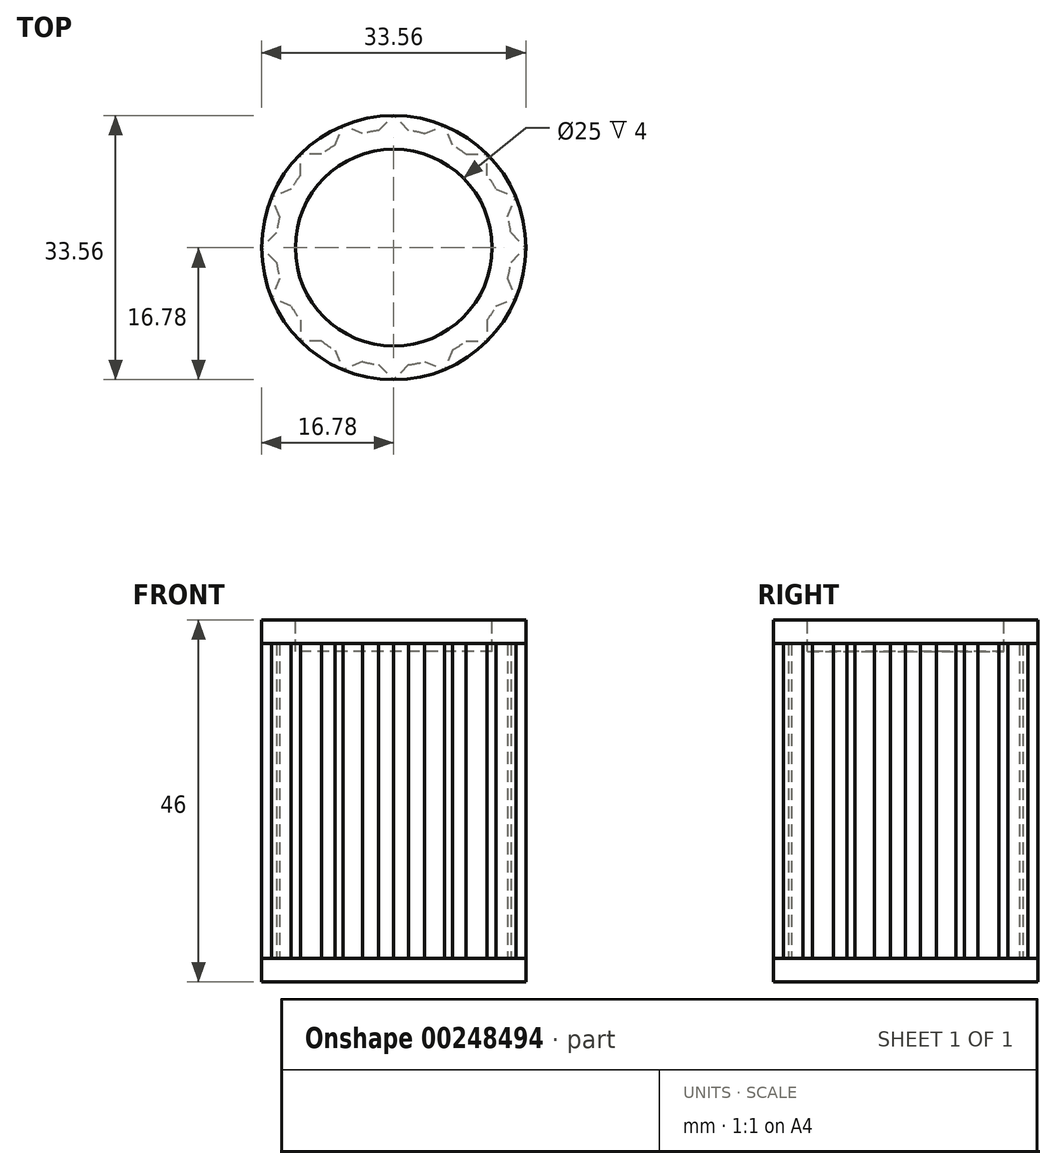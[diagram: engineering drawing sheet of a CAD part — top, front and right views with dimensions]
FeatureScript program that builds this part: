
annotation { "Feature Type Name" : "Feature", "Feature Type Description" : "" }
export const myFeature = defineFeature(function(context is Context, id is Id, definition is map)
    precondition{}
    {
        {
            var Q0;
            Q0=qCreatedBy(makeId("Top.planeOp"),FACE);
            var sketch = newSketch(context, id + "F0", { "sketchPlane" : qUnion([Q0])});
            skCircle(sketch, "E0", {"center": v(0, 0) * mm, "radius": 15 * mm});
            skLineSegment(sketch, "E1", {"start": v(14.28, 0) * mm, "end": v(14.28, 2.5) * mm});
            skLineSegment(sketch, "E2", {"start": v(14.28, 2.5) * mm, "end": v(16.78, 0) * mm});
            skLineSegment(sketch, "E3.MirrorCS", {"start": v(14.28, 0) * mm, "end": v(14.28, -2.5) * mm});
            skLineSegment(sketch, "E4.MirrorCS", {"start": v(14.28, -2.5) * mm, "end": v(16.78, 0) * mm});
            skLineSegment(sketch, "E5.1.0", {"start": v(12.24, 7.77) * mm, "end": v(15.5, 6.42) * mm});
            skLineSegment(sketch, "E5.1.1", {"start": v(14.15, 3.15) * mm, "end": v(15.5, 6.42) * mm});
            skLineSegment(sketch, "E5.1.2", {"start": v(13.2, 5.46) * mm, "end": v(14.15, 3.15) * mm});
            skLineSegment(sketch, "E5.1.3", {"start": v(13.2, 5.46) * mm, "end": v(12.24, 7.77) * mm});
            skLineSegment(sketch, "E5.2.0", {"start": v(8.33, 11.87) * mm, "end": v(11.87, 11.87) * mm});
            skLineSegment(sketch, "E5.2.1", {"start": v(11.87, 8.33) * mm, "end": v(11.87, 11.87) * mm});
            skLineSegment(sketch, "E5.2.2", {"start": v(10.1, 10.1) * mm, "end": v(11.87, 8.33) * mm});
            skLineSegment(sketch, "E5.2.3", {"start": v(10.1, 10.1) * mm, "end": v(8.33, 11.87) * mm});
            skLineSegment(sketch, "E5.3.0", {"start": v(3.15, 14.15) * mm, "end": v(6.42, 15.5) * mm});
            skLineSegment(sketch, "E5.3.1", {"start": v(7.77, 12.24) * mm, "end": v(6.42, 15.5) * mm});
            skLineSegment(sketch, "E5.3.2", {"start": v(5.46, 13.2) * mm, "end": v(7.77, 12.24) * mm});
            skLineSegment(sketch, "E5.3.3", {"start": v(5.46, 13.2) * mm, "end": v(3.15, 14.15) * mm});
            skLineSegment(sketch, "E5.4.0", {"start": v(-2.5, 14.28) * mm, "end": v(0, 16.78) * mm});
            skLineSegment(sketch, "E5.4.1", {"start": v(2.5, 14.28) * mm, "end": v(0, 16.78) * mm});
            skLineSegment(sketch, "E5.4.2", {"start": v(0, 14.28) * mm, "end": v(2.5, 14.28) * mm});
            skLineSegment(sketch, "E5.4.3", {"start": v(0, 14.28) * mm, "end": v(-2.5, 14.28) * mm});
            skLineSegment(sketch, "E5.5.0", {"start": v(-7.77, 12.24) * mm, "end": v(-6.42, 15.5) * mm});
            skLineSegment(sketch, "E5.5.1", {"start": v(-3.15, 14.15) * mm, "end": v(-6.42, 15.5) * mm});
            skLineSegment(sketch, "E5.5.2", {"start": v(-5.46, 13.2) * mm, "end": v(-3.15, 14.15) * mm});
            skLineSegment(sketch, "E5.5.3", {"start": v(-5.46, 13.2) * mm, "end": v(-7.77, 12.24) * mm});
            skLineSegment(sketch, "E5.6.0", {"start": v(-11.87, 8.33) * mm, "end": v(-11.87, 11.87) * mm});
            skLineSegment(sketch, "E5.6.1", {"start": v(-8.33, 11.87) * mm, "end": v(-11.87, 11.87) * mm});
            skLineSegment(sketch, "E5.6.2", {"start": v(-10.1, 10.1) * mm, "end": v(-8.33, 11.87) * mm});
            skLineSegment(sketch, "E5.6.3", {"start": v(-10.1, 10.1) * mm, "end": v(-11.87, 8.33) * mm});
            skLineSegment(sketch, "E5.7.0", {"start": v(-14.15, 3.15) * mm, "end": v(-15.5, 6.42) * mm});
            skLineSegment(sketch, "E5.7.1", {"start": v(-12.24, 7.77) * mm, "end": v(-15.5, 6.42) * mm});
            skLineSegment(sketch, "E5.7.2", {"start": v(-13.2, 5.46) * mm, "end": v(-12.24, 7.77) * mm});
            skLineSegment(sketch, "E5.7.3", {"start": v(-13.2, 5.46) * mm, "end": v(-14.15, 3.15) * mm});
            skLineSegment(sketch, "E5.8.0", {"start": v(-14.28, -2.5) * mm, "end": v(-16.78, 0) * mm});
            skLineSegment(sketch, "E5.8.1", {"start": v(-14.28, 2.5) * mm, "end": v(-16.78, 0) * mm});
            skLineSegment(sketch, "E5.8.2", {"start": v(-14.28, 0) * mm, "end": v(-14.28, 2.5) * mm});
            skLineSegment(sketch, "E5.8.3", {"start": v(-14.28, 0) * mm, "end": v(-14.28, -2.5) * mm});
            skLineSegment(sketch, "E5.9.0", {"start": v(-12.24, -7.77) * mm, "end": v(-15.5, -6.42) * mm});
            skLineSegment(sketch, "E5.9.1", {"start": v(-14.15, -3.15) * mm, "end": v(-15.5, -6.42) * mm});
            skLineSegment(sketch, "E5.9.2", {"start": v(-13.2, -5.46) * mm, "end": v(-14.15, -3.15) * mm});
            skLineSegment(sketch, "E5.9.3", {"start": v(-13.2, -5.46) * mm, "end": v(-12.24, -7.77) * mm});
            skLineSegment(sketch, "E5.10.0", {"start": v(-8.33, -11.87) * mm, "end": v(-11.87, -11.87) * mm});
            skLineSegment(sketch, "E5.10.1", {"start": v(-11.87, -8.33) * mm, "end": v(-11.87, -11.87) * mm});
            skLineSegment(sketch, "E5.10.2", {"start": v(-10.1, -10.1) * mm, "end": v(-11.87, -8.33) * mm});
            skLineSegment(sketch, "E5.10.3", {"start": v(-10.1, -10.1) * mm, "end": v(-8.33, -11.87) * mm});
            skLineSegment(sketch, "E5.11.0", {"start": v(-3.15, -14.15) * mm, "end": v(-6.42, -15.5) * mm});
            skLineSegment(sketch, "E5.11.1", {"start": v(-7.77, -12.24) * mm, "end": v(-6.42, -15.5) * mm});
            skLineSegment(sketch, "E5.11.2", {"start": v(-5.46, -13.2) * mm, "end": v(-7.77, -12.24) * mm});
            skLineSegment(sketch, "E5.11.3", {"start": v(-5.46, -13.2) * mm, "end": v(-3.15, -14.15) * mm});
            skLineSegment(sketch, "E5.12.0", {"start": v(2.5, -14.28) * mm, "end": v(0, -16.78) * mm});
            skLineSegment(sketch, "E5.12.1", {"start": v(-2.5, -14.28) * mm, "end": v(0, -16.78) * mm});
            skLineSegment(sketch, "E5.12.2", {"start": v(0, -14.28) * mm, "end": v(-2.5, -14.28) * mm});
            skLineSegment(sketch, "E5.12.3", {"start": v(0, -14.28) * mm, "end": v(2.5, -14.28) * mm});
            skLineSegment(sketch, "E5.13.0", {"start": v(7.77, -12.24) * mm, "end": v(6.42, -15.5) * mm});
            skLineSegment(sketch, "E5.13.1", {"start": v(3.15, -14.15) * mm, "end": v(6.42, -15.5) * mm});
            skLineSegment(sketch, "E5.13.2", {"start": v(5.46, -13.2) * mm, "end": v(3.15, -14.15) * mm});
            skLineSegment(sketch, "E5.13.3", {"start": v(5.46, -13.2) * mm, "end": v(7.77, -12.24) * mm});
            skLineSegment(sketch, "E5.14.0", {"start": v(11.87, -8.33) * mm, "end": v(11.87, -11.87) * mm});
            skLineSegment(sketch, "E5.14.1", {"start": v(8.33, -11.87) * mm, "end": v(11.87, -11.87) * mm});
            skLineSegment(sketch, "E5.14.2", {"start": v(10.1, -10.1) * mm, "end": v(8.33, -11.87) * mm});
            skLineSegment(sketch, "E5.14.3", {"start": v(10.1, -10.1) * mm, "end": v(11.87, -8.33) * mm});
            skLineSegment(sketch, "E5.15.0", {"start": v(14.15, -3.15) * mm, "end": v(15.5, -6.42) * mm});
            skLineSegment(sketch, "E5.15.1", {"start": v(12.24, -7.77) * mm, "end": v(15.5, -6.42) * mm});
            skLineSegment(sketch, "E5.15.2", {"start": v(13.2, -5.46) * mm, "end": v(12.24, -7.77) * mm});
            skLineSegment(sketch, "E5.15.3", {"start": v(13.2, -5.46) * mm, "end": v(14.15, -3.15) * mm});
            skSolve(sketch);
        }
        {
            var Q0;
            {var subQ0=sQuery(id+"F0.wireOp",EDGE,"E5.6.2");Q0=makeQuery(id+"F0.imprint","IMPRINT",FACE,{"disambiguationData":[TD([[makeQuery(id+"F0.imprint","IMPRINT",EDGE,{"derivedFrom":subQ0}),1.0]])]});}
            var Q1;
            {var subQ0=sQuery(id+"F0.wireOp",EDGE,"E5.5.2");Q1=makeQuery(id+"F0.imprint","IMPRINT",FACE,{"disambiguationData":[TD([[makeQuery(id+"F0.imprint","IMPRINT",EDGE,{"derivedFrom":subQ0}),1.0]])]});}
            var Q2;
            {var subQ0=sQuery(id+"F0.wireOp",EDGE,"E5.4.2");Q2=makeQuery(id+"F0.imprint","IMPRINT",FACE,{"disambiguationData":[TD([[makeQuery(id+"F0.imprint","IMPRINT",EDGE,{"derivedFrom":subQ0}),1.0]])]});}
            var Q3;
            {var subQ0=sQuery(id+"F0.wireOp",EDGE,"E5.3.2");Q3=makeQuery(id+"F0.imprint","IMPRINT",FACE,{"disambiguationData":[TD([[makeQuery(id+"F0.imprint","IMPRINT",EDGE,{"derivedFrom":subQ0}),1.0]])]});}
            var Q4;
            {var subQ0=sQuery(id+"F0.wireOp",EDGE,"E5.2.2");Q4=makeQuery(id+"F0.imprint","IMPRINT",FACE,{"disambiguationData":[TD([[makeQuery(id+"F0.imprint","IMPRINT",EDGE,{"derivedFrom":subQ0}),1.0]])]});}
            var Q5;
            {var subQ2=sQuery(id+"F0.wireOp",EDGE,"E1");Q5=makeQuery(id+"F0.imprint","IMPRINT",FACE,{"disambiguationData":[TD([[makeQuery(id+"F0.imprint","IMPRINT",EDGE,{"derivedFrom":subQ2}),-1.0]])]});}
            var Q6;
            {var subQ0=sQuery(id+"F0.wireOp",EDGE,"E5.15.2");Q6=makeQuery(id+"F0.imprint","IMPRINT",FACE,{"disambiguationData":[TD([[makeQuery(id+"F0.imprint","IMPRINT",EDGE,{"derivedFrom":subQ0}),1.0]])]});}
            var Q7;
            {var subQ0=sQuery(id+"F0.wireOp",EDGE,"E5.14.2");Q7=makeQuery(id+"F0.imprint","IMPRINT",FACE,{"disambiguationData":[TD([[makeQuery(id+"F0.imprint","IMPRINT",EDGE,{"derivedFrom":subQ0}),1.0]])]});}
            var Q8;
            {var subQ0=sQuery(id+"F0.wireOp",EDGE,"E5.13.2");Q8=makeQuery(id+"F0.imprint","IMPRINT",FACE,{"disambiguationData":[TD([[makeQuery(id+"F0.imprint","IMPRINT",EDGE,{"derivedFrom":subQ0}),1.0]])]});}
            var Q9;
            {var subQ0=sQuery(id+"F0.wireOp",EDGE,"E5.12.2");Q9=makeQuery(id+"F0.imprint","IMPRINT",FACE,{"disambiguationData":[TD([[makeQuery(id+"F0.imprint","IMPRINT",EDGE,{"derivedFrom":subQ0}),1.0]])]});}
            var Q10;
            {var subQ0=sQuery(id+"F0.wireOp",EDGE,"E5.11.2");Q10=makeQuery(id+"F0.imprint","IMPRINT",FACE,{"disambiguationData":[TD([[makeQuery(id+"F0.imprint","IMPRINT",EDGE,{"derivedFrom":subQ0}),1.0]])]});}
            var Q11;
            {var subQ0=sQuery(id+"F0.wireOp",EDGE,"E5.10.2");Q11=makeQuery(id+"F0.imprint","IMPRINT",FACE,{"disambiguationData":[TD([[makeQuery(id+"F0.imprint","IMPRINT",EDGE,{"derivedFrom":subQ0}),1.0]])]});}
            var Q12;
            {var subQ0=sQuery(id+"F0.wireOp",EDGE,"E5.9.2");Q12=makeQuery(id+"F0.imprint","IMPRINT",FACE,{"disambiguationData":[TD([[makeQuery(id+"F0.imprint","IMPRINT",EDGE,{"derivedFrom":subQ0}),1.0]])]});}
            var Q13;
            {var subQ0=sQuery(id+"F0.wireOp",EDGE,"E5.8.2");Q13=makeQuery(id+"F0.imprint","IMPRINT",FACE,{"disambiguationData":[TD([[makeQuery(id+"F0.imprint","IMPRINT",EDGE,{"derivedFrom":subQ0}),1.0]])]});}
            var Q14;
            {var subQ0=sQuery(id+"F0.wireOp",EDGE,"E5.7.2");Q14=makeQuery(id+"F0.imprint","IMPRINT",FACE,{"disambiguationData":[TD([[makeQuery(id+"F0.imprint","IMPRINT",EDGE,{"derivedFrom":subQ0}),1.0]])]});}
            var Q15;
            {var subQ79=sQuery(id+"F0.wireOp",EDGE,"E1");Q15=makeQuery(id+"F0.imprint","IMPRINT",FACE,{"disambiguationData":[TD([[makeQuery(id+"F0.imprint","IMPRINT",EDGE,{"derivedFrom":subQ79}),1.0]])]});}
            var Q16;
            {var subQ0=sQuery(id+"F0.wireOp",EDGE,"E5.1.2");Q16=makeQuery(id+"F0.imprint","IMPRINT",FACE,{"disambiguationData":[TD([[makeQuery(id+"F0.imprint","IMPRINT",EDGE,{"derivedFrom":subQ0}),1.0]])]});}
            var Q17;
            {var subQ0=sQuery(id+"F0.wireOp",EDGE,"E5.13.1");var subQ1=sQuery(id+"F0.wireOp",EDGE,"E0");var subQ2=makeQuery(id+"F0.imprint","INTERSECT",VERTEX,{"derivedFrom":[subQ1,subQ0]});Q17=makeQuery(id+"F0.imprint","IMPRINT",FACE,{"disambiguationData":[TD([[makeQuery(id+"F0.imprint","IMPRINT",EDGE,{"disambiguationData":[TD([[subQ2,-1.0]])],"derivedFrom":subQ1}),-1.0]])]});}
            var Q18;
            {var subQ0=sQuery(id+"F0.wireOp",EDGE,"E5.14.1");var subQ1=sQuery(id+"F0.wireOp",EDGE,"E0");var subQ2=makeQuery(id+"F0.imprint","INTERSECT",VERTEX,{"derivedFrom":[subQ1,subQ0]});Q18=makeQuery(id+"F0.imprint","IMPRINT",FACE,{"disambiguationData":[TD([[makeQuery(id+"F0.imprint","IMPRINT",EDGE,{"disambiguationData":[TD([[subQ2,-1.0]])],"derivedFrom":subQ1}),-1.0]])]});}
            var Q19;
            {var subQ0=sQuery(id+"F0.wireOp",EDGE,"E5.12.1");var subQ1=sQuery(id+"F0.wireOp",EDGE,"E0");var subQ2=makeQuery(id+"F0.imprint","INTERSECT",VERTEX,{"derivedFrom":[subQ1,subQ0]});Q19=makeQuery(id+"F0.imprint","IMPRINT",FACE,{"disambiguationData":[TD([[makeQuery(id+"F0.imprint","IMPRINT",EDGE,{"disambiguationData":[TD([[subQ2,-1.0]])],"derivedFrom":subQ1}),-1.0]])]});}
            var Q20;
            {var subQ0=sQuery(id+"F0.wireOp",EDGE,"E5.11.1");var subQ1=sQuery(id+"F0.wireOp",EDGE,"E0");var subQ2=makeQuery(id+"F0.imprint","INTERSECT",VERTEX,{"derivedFrom":[subQ1,subQ0]});Q20=makeQuery(id+"F0.imprint","IMPRINT",FACE,{"disambiguationData":[TD([[makeQuery(id+"F0.imprint","IMPRINT",EDGE,{"disambiguationData":[TD([[subQ2,-1.0]])],"derivedFrom":subQ1}),-1.0]])]});}
            var Q21;
            {var subQ0=sQuery(id+"F0.wireOp",EDGE,"E5.10.1");var subQ1=sQuery(id+"F0.wireOp",EDGE,"E0");var subQ2=makeQuery(id+"F0.imprint","INTERSECT",VERTEX,{"derivedFrom":[subQ1,subQ0]});Q21=makeQuery(id+"F0.imprint","IMPRINT",FACE,{"disambiguationData":[TD([[makeQuery(id+"F0.imprint","IMPRINT",EDGE,{"disambiguationData":[TD([[subQ2,-1.0]])],"derivedFrom":subQ1}),-1.0]])]});}
            var Q22;
            {var subQ0=sQuery(id+"F0.wireOp",EDGE,"E5.9.1");var subQ1=sQuery(id+"F0.wireOp",EDGE,"E0");var subQ2=makeQuery(id+"F0.imprint","INTERSECT",VERTEX,{"derivedFrom":[subQ1,subQ0]});Q22=makeQuery(id+"F0.imprint","IMPRINT",FACE,{"disambiguationData":[TD([[makeQuery(id+"F0.imprint","IMPRINT",EDGE,{"disambiguationData":[TD([[subQ2,-1.0]])],"derivedFrom":subQ1}),-1.0]])]});}
            var Q23;
            {var subQ0=sQuery(id+"F0.wireOp",EDGE,"E5.8.1");var subQ1=sQuery(id+"F0.wireOp",EDGE,"E0");var subQ2=makeQuery(id+"F0.imprint","INTERSECT",VERTEX,{"derivedFrom":[subQ1,subQ0]});Q23=makeQuery(id+"F0.imprint","IMPRINT",FACE,{"disambiguationData":[TD([[makeQuery(id+"F0.imprint","IMPRINT",EDGE,{"disambiguationData":[TD([[subQ2,-1.0]])],"derivedFrom":subQ1}),-1.0]])]});}
            var Q24;
            {var subQ0=sQuery(id+"F0.wireOp",EDGE,"E5.7.1");var subQ1=sQuery(id+"F0.wireOp",EDGE,"E0");var subQ2=makeQuery(id+"F0.imprint","INTERSECT",VERTEX,{"derivedFrom":[subQ1,subQ0]});Q24=makeQuery(id+"F0.imprint","IMPRINT",FACE,{"disambiguationData":[TD([[makeQuery(id+"F0.imprint","IMPRINT",EDGE,{"disambiguationData":[TD([[subQ2,-1.0]])],"derivedFrom":subQ1}),-1.0]])]});}
            var Q25;
            {var subQ0=sQuery(id+"F0.wireOp",EDGE,"E5.6.1");var subQ1=sQuery(id+"F0.wireOp",EDGE,"E0");var subQ2=makeQuery(id+"F0.imprint","INTERSECT",VERTEX,{"derivedFrom":[subQ1,subQ0]});Q25=makeQuery(id+"F0.imprint","IMPRINT",FACE,{"disambiguationData":[TD([[makeQuery(id+"F0.imprint","IMPRINT",EDGE,{"disambiguationData":[TD([[subQ2,-1.0]])],"derivedFrom":subQ1}),-1.0]])]});}
            var Q26;
            {var subQ0=sQuery(id+"F0.wireOp",EDGE,"E5.5.1");var subQ1=sQuery(id+"F0.wireOp",EDGE,"E0");var subQ2=makeQuery(id+"F0.imprint","INTERSECT",VERTEX,{"derivedFrom":[subQ1,subQ0]});Q26=makeQuery(id+"F0.imprint","IMPRINT",FACE,{"disambiguationData":[TD([[makeQuery(id+"F0.imprint","IMPRINT",EDGE,{"disambiguationData":[TD([[subQ2,-1.0]])],"derivedFrom":subQ1}),-1.0]])]});}
            var Q27;
            {var subQ0=sQuery(id+"F0.wireOp",EDGE,"E5.4.1");var subQ1=sQuery(id+"F0.wireOp",EDGE,"E0");var subQ2=makeQuery(id+"F0.imprint","INTERSECT",VERTEX,{"derivedFrom":[subQ1,subQ0]});Q27=makeQuery(id+"F0.imprint","IMPRINT",FACE,{"disambiguationData":[TD([[makeQuery(id+"F0.imprint","IMPRINT",EDGE,{"disambiguationData":[TD([[subQ2,-1.0]])],"derivedFrom":subQ1}),-1.0]])]});}
            var Q28;
            {var subQ0=sQuery(id+"F0.wireOp",EDGE,"E5.3.1");var subQ1=sQuery(id+"F0.wireOp",EDGE,"E0");var subQ2=makeQuery(id+"F0.imprint","INTERSECT",VERTEX,{"derivedFrom":[subQ1,subQ0]});Q28=makeQuery(id+"F0.imprint","IMPRINT",FACE,{"disambiguationData":[TD([[makeQuery(id+"F0.imprint","IMPRINT",EDGE,{"disambiguationData":[TD([[subQ2,-1.0]])],"derivedFrom":subQ1}),-1.0]])]});}
            var Q29;
            {var subQ0=sQuery(id+"F0.wireOp",EDGE,"E5.2.1");var subQ1=sQuery(id+"F0.wireOp",EDGE,"E0");var subQ2=makeQuery(id+"F0.imprint","INTERSECT",VERTEX,{"derivedFrom":[subQ1,subQ0]});Q29=makeQuery(id+"F0.imprint","IMPRINT",FACE,{"disambiguationData":[TD([[makeQuery(id+"F0.imprint","IMPRINT",EDGE,{"disambiguationData":[TD([[subQ2,-1.0]])],"derivedFrom":subQ1}),-1.0]])]});}
            var Q30;
            {var subQ0=sQuery(id+"F0.wireOp",EDGE,"E5.1.1");var subQ1=sQuery(id+"F0.wireOp",EDGE,"E0");var subQ2=makeQuery(id+"F0.imprint","INTERSECT",VERTEX,{"derivedFrom":[subQ1,subQ0]});Q30=makeQuery(id+"F0.imprint","IMPRINT",FACE,{"disambiguationData":[TD([[makeQuery(id+"F0.imprint","IMPRINT",EDGE,{"disambiguationData":[TD([[subQ2,-1.0]])],"derivedFrom":subQ1}),-1.0]])]});}
            var Q31;
            {var subQ0=sQuery(id+"F0.wireOp",EDGE,"E2");var subQ1=sQuery(id+"F0.wireOp",EDGE,"E0");var subQ2=makeQuery(id+"F0.imprint","INTERSECT",VERTEX,{"derivedFrom":[subQ1,subQ0]});Q31=makeQuery(id+"F0.imprint","IMPRINT",FACE,{"disambiguationData":[TD([[makeQuery(id+"F0.imprint","IMPRINT",EDGE,{"disambiguationData":[TD([[subQ2,1.0]])],"derivedFrom":subQ1}),-1.0]])]});}
            var Q32;
            {var subQ0=sQuery(id+"F0.wireOp",EDGE,"E5.15.1");var subQ1=sQuery(id+"F0.wireOp",EDGE,"E0");var subQ2=makeQuery(id+"F0.imprint","INTERSECT",VERTEX,{"derivedFrom":[subQ1,subQ0]});Q32=makeQuery(id+"F0.imprint","IMPRINT",FACE,{"disambiguationData":[TD([[makeQuery(id+"F0.imprint","IMPRINT",EDGE,{"disambiguationData":[TD([[subQ2,-1.0]])],"derivedFrom":subQ1}),-1.0]])]});}
            extrude(context, id + "F1", {"entities" : qUnion([Q0, Q1, Q2, Q3, Q4, Q5, Q6, Q7, Q8, Q9, Q10, Q11, Q12, Q13, Q14, Q15, Q16, Q17, Q18, Q19, Q20, Q21, Q22, Q23, Q24, Q25, Q26, Q27, Q28, Q29, Q30, Q31, Q32]), "depth" : 40 * mm});
        }
        {
            var Q0;
            Q0=makeQuery(id+"F1.opExtrude","CAP_FACE",FACE,{"disambiguationData":[OSD([sQuery(id+"F0.wireOp",EDGE,"E0"),sQuery(id+"F0.wireOp",EDGE,"E2"),sQuery(id+"F0.wireOp",EDGE,"E4.MirrorCS"),sQuery(id+"F0.wireOp",EDGE,"E5.1.0"),sQuery(id+"F0.wireOp",EDGE,"E5.1.1"),sQuery(id+"F0.wireOp",EDGE,"E5.2.0"),sQuery(id+"F0.wireOp",EDGE,"E5.2.1"),sQuery(id+"F0.wireOp",EDGE,"E5.3.0"),sQuery(id+"F0.wireOp",EDGE,"E5.3.1"),sQuery(id+"F0.wireOp",EDGE,"E5.4.0"),sQuery(id+"F0.wireOp",EDGE,"E5.4.1"),sQuery(id+"F0.wireOp",EDGE,"E5.5.0"),sQuery(id+"F0.wireOp",EDGE,"E5.5.1"),sQuery(id+"F0.wireOp",EDGE,"E5.6.0"),sQuery(id+"F0.wireOp",EDGE,"E5.6.1"),sQuery(id+"F0.wireOp",EDGE,"E5.7.0"),sQuery(id+"F0.wireOp",EDGE,"E5.7.1"),sQuery(id+"F0.wireOp",EDGE,"E5.8.0"),sQuery(id+"F0.wireOp",EDGE,"E5.8.1"),sQuery(id+"F0.wireOp",EDGE,"E5.9.0"),sQuery(id+"F0.wireOp",EDGE,"E5.9.1"),sQuery(id+"F0.wireOp",EDGE,"E5.10.0"),sQuery(id+"F0.wireOp",EDGE,"E5.10.1"),sQuery(id+"F0.wireOp",EDGE,"E5.11.0"),sQuery(id+"F0.wireOp",EDGE,"E5.11.1"),sQuery(id+"F0.wireOp",EDGE,"E5.12.0"),sQuery(id+"F0.wireOp",EDGE,"E5.12.1"),sQuery(id+"F0.wireOp",EDGE,"E5.13.0"),sQuery(id+"F0.wireOp",EDGE,"E5.13.1"),sQuery(id+"F0.wireOp",EDGE,"E5.14.0"),sQuery(id+"F0.wireOp",EDGE,"E5.14.1"),sQuery(id+"F0.wireOp",EDGE,"E5.15.0"),sQuery(id+"F0.wireOp",EDGE,"E5.15.1")])],"isStart":false});
            var sketch = newSketch(context, id + "F2", { "sketchPlane" : qUnion([Q0])});
            skCircle(sketch, "E6", {"center": v(0, 0) * mm, "radius": 16.78 * mm});
            skSolve(sketch);
        }
        {
            var Q0;
            {var subQ23=sQuery(id+"F0.wireOp",EDGE,"E2");Q0=makeQuery(id+"F2.imprint","IMPRINT",FACE,{"disambiguationData":[TD([[makeQuery(id+"F2.imprint","IMPRINT",EDGE,{"derivedFrom":makeQuery(id+"F1.opExtrude","CAP_EDGE",EDGE,{"disambiguationData":[OSD([subQ23])],"isStart":false})}),-1.0]])]});}
            var Q1;
            {var subQ1=sQuery(id+"F0.wireOp",EDGE,"E5.10.0");var subQ2=makeQuery(id+"F1.opExtrude","CAP_EDGE",EDGE,{"disambiguationData":[OSD([subQ1])],"isStart":false});Q1=makeQuery(id+"F2.imprint","IMPRINT",FACE,{"disambiguationData":[TD([[makeQuery(id+"F2.imprint","IMPRINT",EDGE,{"derivedFrom":subQ2}),1.0]])]});}
            var Q2;
            {var subQ1=sQuery(id+"F0.wireOp",EDGE,"E5.11.0");var subQ2=makeQuery(id+"F1.opExtrude","CAP_EDGE",EDGE,{"disambiguationData":[OSD([subQ1])],"isStart":false});Q2=makeQuery(id+"F2.imprint","IMPRINT",FACE,{"disambiguationData":[TD([[makeQuery(id+"F2.imprint","IMPRINT",EDGE,{"derivedFrom":subQ2}),1.0]])]});}
            var Q3;
            {var subQ1=sQuery(id+"F0.wireOp",EDGE,"E5.12.0");var subQ2=makeQuery(id+"F1.opExtrude","CAP_EDGE",EDGE,{"disambiguationData":[OSD([subQ1])],"isStart":false});Q3=makeQuery(id+"F2.imprint","IMPRINT",FACE,{"disambiguationData":[TD([[makeQuery(id+"F2.imprint","IMPRINT",EDGE,{"derivedFrom":subQ2}),1.0]])]});}
            var Q4;
            {var subQ1=sQuery(id+"F0.wireOp",EDGE,"E5.13.0");var subQ2=makeQuery(id+"F1.opExtrude","CAP_EDGE",EDGE,{"disambiguationData":[OSD([subQ1])],"isStart":false});Q4=makeQuery(id+"F2.imprint","IMPRINT",FACE,{"disambiguationData":[TD([[makeQuery(id+"F2.imprint","IMPRINT",EDGE,{"derivedFrom":subQ2}),1.0]])]});}
            var Q5;
            {var subQ1=sQuery(id+"F0.wireOp",EDGE,"E5.14.0");var subQ2=makeQuery(id+"F1.opExtrude","CAP_EDGE",EDGE,{"disambiguationData":[OSD([subQ1])],"isStart":false});Q5=makeQuery(id+"F2.imprint","IMPRINT",FACE,{"disambiguationData":[TD([[makeQuery(id+"F2.imprint","IMPRINT",EDGE,{"derivedFrom":subQ2}),1.0]])]});}
            var Q6;
            {var subQ1=sQuery(id+"F0.wireOp",EDGE,"E4.MirrorCS");var subQ2=makeQuery(id+"F1.opExtrude","CAP_EDGE",EDGE,{"disambiguationData":[OSD([subQ1])],"isStart":false});Q6=makeQuery(id+"F2.imprint","IMPRINT",FACE,{"disambiguationData":[TD([[makeQuery(id+"F2.imprint","IMPRINT",EDGE,{"derivedFrom":subQ2}),-1.0]])]});}
            var Q7;
            {var subQ1=sQuery(id+"F0.wireOp",EDGE,"E2");var subQ2=makeQuery(id+"F1.opExtrude","CAP_EDGE",EDGE,{"disambiguationData":[OSD([subQ1])],"isStart":false});Q7=makeQuery(id+"F2.imprint","IMPRINT",FACE,{"disambiguationData":[TD([[makeQuery(id+"F2.imprint","IMPRINT",EDGE,{"derivedFrom":subQ2}),1.0]])]});}
            var Q8;
            {var subQ1=sQuery(id+"F0.wireOp",EDGE,"E5.1.0");var subQ2=makeQuery(id+"F1.opExtrude","CAP_EDGE",EDGE,{"disambiguationData":[OSD([subQ1])],"isStart":false});Q8=makeQuery(id+"F2.imprint","IMPRINT",FACE,{"disambiguationData":[TD([[makeQuery(id+"F2.imprint","IMPRINT",EDGE,{"derivedFrom":subQ2}),1.0]])]});}
            var Q9;
            {var subQ1=sQuery(id+"F0.wireOp",EDGE,"E5.2.0");var subQ2=makeQuery(id+"F1.opExtrude","CAP_EDGE",EDGE,{"disambiguationData":[OSD([subQ1])],"isStart":false});Q9=makeQuery(id+"F2.imprint","IMPRINT",FACE,{"disambiguationData":[TD([[makeQuery(id+"F2.imprint","IMPRINT",EDGE,{"derivedFrom":subQ2}),1.0]])]});}
            var Q10;
            {var subQ1=sQuery(id+"F0.wireOp",EDGE,"E5.9.0");var subQ2=makeQuery(id+"F1.opExtrude","CAP_EDGE",EDGE,{"disambiguationData":[OSD([subQ1])],"isStart":false});Q10=makeQuery(id+"F2.imprint","IMPRINT",FACE,{"disambiguationData":[TD([[makeQuery(id+"F2.imprint","IMPRINT",EDGE,{"derivedFrom":subQ2}),1.0]])]});}
            var Q11;
            {var subQ1=sQuery(id+"F0.wireOp",EDGE,"E5.8.0");var subQ2=makeQuery(id+"F1.opExtrude","CAP_EDGE",EDGE,{"disambiguationData":[OSD([subQ1])],"isStart":false});Q11=makeQuery(id+"F2.imprint","IMPRINT",FACE,{"disambiguationData":[TD([[makeQuery(id+"F2.imprint","IMPRINT",EDGE,{"derivedFrom":subQ2}),1.0]])]});}
            var Q12;
            {var subQ1=sQuery(id+"F0.wireOp",EDGE,"E5.7.0");var subQ2=makeQuery(id+"F1.opExtrude","CAP_EDGE",EDGE,{"disambiguationData":[OSD([subQ1])],"isStart":false});Q12=makeQuery(id+"F2.imprint","IMPRINT",FACE,{"disambiguationData":[TD([[makeQuery(id+"F2.imprint","IMPRINT",EDGE,{"derivedFrom":subQ2}),1.0]])]});}
            var Q13;
            {var subQ1=sQuery(id+"F0.wireOp",EDGE,"E5.6.0");var subQ2=makeQuery(id+"F1.opExtrude","CAP_EDGE",EDGE,{"disambiguationData":[OSD([subQ1])],"isStart":false});Q13=makeQuery(id+"F2.imprint","IMPRINT",FACE,{"disambiguationData":[TD([[makeQuery(id+"F2.imprint","IMPRINT",EDGE,{"derivedFrom":subQ2}),1.0]])]});}
            var Q14;
            {var subQ1=sQuery(id+"F0.wireOp",EDGE,"E5.5.0");var subQ2=makeQuery(id+"F1.opExtrude","CAP_EDGE",EDGE,{"disambiguationData":[OSD([subQ1])],"isStart":false});Q14=makeQuery(id+"F2.imprint","IMPRINT",FACE,{"disambiguationData":[TD([[makeQuery(id+"F2.imprint","IMPRINT",EDGE,{"derivedFrom":subQ2}),1.0]])]});}
            var Q15;
            {var subQ1=sQuery(id+"F0.wireOp",EDGE,"E5.4.0");var subQ2=makeQuery(id+"F1.opExtrude","CAP_EDGE",EDGE,{"disambiguationData":[OSD([subQ1])],"isStart":false});Q15=makeQuery(id+"F2.imprint","IMPRINT",FACE,{"disambiguationData":[TD([[makeQuery(id+"F2.imprint","IMPRINT",EDGE,{"derivedFrom":subQ2}),1.0]])]});}
            var Q16;
            {var subQ1=sQuery(id+"F0.wireOp",EDGE,"E5.3.0");var subQ2=makeQuery(id+"F1.opExtrude","CAP_EDGE",EDGE,{"disambiguationData":[OSD([subQ1])],"isStart":false});Q16=makeQuery(id+"F2.imprint","IMPRINT",FACE,{"disambiguationData":[TD([[makeQuery(id+"F2.imprint","IMPRINT",EDGE,{"derivedFrom":subQ2}),1.0]])]});}
            extrude(context, id + "F3", {"entities" : qUnion([Q0, Q1, Q2, Q3, Q4, Q5, Q6, Q7, Q8, Q9, Q10, Q11, Q12, Q13, Q14, Q15, Q16]), "operationType" : NewBodyOperationType.ADD, "depth" : 3 * mm});
        }
        {
            var Q0;
            Q0=makeQuery(id+"F1.opExtrude","CAP_FACE",FACE,{"disambiguationData":[OSD([sQuery(id+"F0.wireOp",EDGE,"E0"),sQuery(id+"F0.wireOp",EDGE,"E2"),sQuery(id+"F0.wireOp",EDGE,"E4.MirrorCS"),sQuery(id+"F0.wireOp",EDGE,"E5.1.0"),sQuery(id+"F0.wireOp",EDGE,"E5.1.1"),sQuery(id+"F0.wireOp",EDGE,"E5.2.0"),sQuery(id+"F0.wireOp",EDGE,"E5.2.1"),sQuery(id+"F0.wireOp",EDGE,"E5.3.0"),sQuery(id+"F0.wireOp",EDGE,"E5.3.1"),sQuery(id+"F0.wireOp",EDGE,"E5.4.0"),sQuery(id+"F0.wireOp",EDGE,"E5.4.1"),sQuery(id+"F0.wireOp",EDGE,"E5.5.0"),sQuery(id+"F0.wireOp",EDGE,"E5.5.1"),sQuery(id+"F0.wireOp",EDGE,"E5.6.0"),sQuery(id+"F0.wireOp",EDGE,"E5.6.1"),sQuery(id+"F0.wireOp",EDGE,"E5.7.0"),sQuery(id+"F0.wireOp",EDGE,"E5.7.1"),sQuery(id+"F0.wireOp",EDGE,"E5.8.0"),sQuery(id+"F0.wireOp",EDGE,"E5.8.1"),sQuery(id+"F0.wireOp",EDGE,"E5.9.0"),sQuery(id+"F0.wireOp",EDGE,"E5.9.1"),sQuery(id+"F0.wireOp",EDGE,"E5.10.0"),sQuery(id+"F0.wireOp",EDGE,"E5.10.1"),sQuery(id+"F0.wireOp",EDGE,"E5.11.0"),sQuery(id+"F0.wireOp",EDGE,"E5.11.1"),sQuery(id+"F0.wireOp",EDGE,"E5.12.0"),sQuery(id+"F0.wireOp",EDGE,"E5.12.1"),sQuery(id+"F0.wireOp",EDGE,"E5.13.0"),sQuery(id+"F0.wireOp",EDGE,"E5.13.1"),sQuery(id+"F0.wireOp",EDGE,"E5.14.0"),sQuery(id+"F0.wireOp",EDGE,"E5.14.1"),sQuery(id+"F0.wireOp",EDGE,"E5.15.0"),sQuery(id+"F0.wireOp",EDGE,"E5.15.1")])],"isStart":true});
            var sketch = newSketch(context, id + "F4", { "sketchPlane" : qUnion([Q0])});
            skCircle(sketch, "E7", {"center": v(0, 0) * mm, "radius": 16.78 * mm});
            skSolve(sketch);
        }
        {
            var Q0;
            {var subQ1=sQuery(id+"F0.wireOp",EDGE,"E5.12.0");var subQ2=makeQuery(id+"F1.opExtrude","CAP_EDGE",EDGE,{"disambiguationData":[OSD([subQ1])],"isStart":true});Q0=makeQuery(id+"F4.imprint","IMPRINT",FACE,{"disambiguationData":[TD([[makeQuery(id+"F4.imprint","IMPRINT",EDGE,{"derivedFrom":subQ2}),-1.0]])]});}
            var Q1;
            {var subQ1=sQuery(id+"F0.wireOp",EDGE,"E5.11.0");var subQ2=makeQuery(id+"F1.opExtrude","CAP_EDGE",EDGE,{"disambiguationData":[OSD([subQ1])],"isStart":true});Q1=makeQuery(id+"F4.imprint","IMPRINT",FACE,{"disambiguationData":[TD([[makeQuery(id+"F4.imprint","IMPRINT",EDGE,{"derivedFrom":subQ2}),-1.0]])]});}
            var Q2;
            {var subQ1=sQuery(id+"F0.wireOp",EDGE,"E5.10.0");var subQ2=makeQuery(id+"F1.opExtrude","CAP_EDGE",EDGE,{"disambiguationData":[OSD([subQ1])],"isStart":true});Q2=makeQuery(id+"F4.imprint","IMPRINT",FACE,{"disambiguationData":[TD([[makeQuery(id+"F4.imprint","IMPRINT",EDGE,{"derivedFrom":subQ2}),-1.0]])]});}
            var Q3;
            {var subQ1=sQuery(id+"F0.wireOp",EDGE,"E5.9.0");var subQ2=makeQuery(id+"F1.opExtrude","CAP_EDGE",EDGE,{"disambiguationData":[OSD([subQ1])],"isStart":true});Q3=makeQuery(id+"F4.imprint","IMPRINT",FACE,{"disambiguationData":[TD([[makeQuery(id+"F4.imprint","IMPRINT",EDGE,{"derivedFrom":subQ2}),-1.0]])]});}
            var Q4;
            {var subQ1=sQuery(id+"F0.wireOp",EDGE,"E5.8.0");var subQ2=makeQuery(id+"F1.opExtrude","CAP_EDGE",EDGE,{"disambiguationData":[OSD([subQ1])],"isStart":true});Q4=makeQuery(id+"F4.imprint","IMPRINT",FACE,{"disambiguationData":[TD([[makeQuery(id+"F4.imprint","IMPRINT",EDGE,{"derivedFrom":subQ2}),-1.0]])]});}
            var Q5;
            {var subQ1=sQuery(id+"F0.wireOp",EDGE,"E5.7.0");var subQ2=makeQuery(id+"F1.opExtrude","CAP_EDGE",EDGE,{"disambiguationData":[OSD([subQ1])],"isStart":true});Q5=makeQuery(id+"F4.imprint","IMPRINT",FACE,{"disambiguationData":[TD([[makeQuery(id+"F4.imprint","IMPRINT",EDGE,{"derivedFrom":subQ2}),-1.0]])]});}
            var Q6;
            {var subQ1=sQuery(id+"F0.wireOp",EDGE,"E5.6.0");var subQ2=makeQuery(id+"F1.opExtrude","CAP_EDGE",EDGE,{"disambiguationData":[OSD([subQ1])],"isStart":true});Q6=makeQuery(id+"F4.imprint","IMPRINT",FACE,{"disambiguationData":[TD([[makeQuery(id+"F4.imprint","IMPRINT",EDGE,{"derivedFrom":subQ2}),-1.0]])]});}
            var Q7;
            {var subQ1=sQuery(id+"F0.wireOp",EDGE,"E5.5.0");var subQ2=makeQuery(id+"F1.opExtrude","CAP_EDGE",EDGE,{"disambiguationData":[OSD([subQ1])],"isStart":true});Q7=makeQuery(id+"F4.imprint","IMPRINT",FACE,{"disambiguationData":[TD([[makeQuery(id+"F4.imprint","IMPRINT",EDGE,{"derivedFrom":subQ2}),-1.0]])]});}
            var Q8;
            {var subQ1=sQuery(id+"F0.wireOp",EDGE,"E5.4.0");var subQ2=makeQuery(id+"F1.opExtrude","CAP_EDGE",EDGE,{"disambiguationData":[OSD([subQ1])],"isStart":true});Q8=makeQuery(id+"F4.imprint","IMPRINT",FACE,{"disambiguationData":[TD([[makeQuery(id+"F4.imprint","IMPRINT",EDGE,{"derivedFrom":subQ2}),-1.0]])]});}
            var Q9;
            {var subQ1=sQuery(id+"F0.wireOp",EDGE,"E5.3.0");var subQ2=makeQuery(id+"F1.opExtrude","CAP_EDGE",EDGE,{"disambiguationData":[OSD([subQ1])],"isStart":true});Q9=makeQuery(id+"F4.imprint","IMPRINT",FACE,{"disambiguationData":[TD([[makeQuery(id+"F4.imprint","IMPRINT",EDGE,{"derivedFrom":subQ2}),-1.0]])]});}
            var Q10;
            {var subQ1=sQuery(id+"F0.wireOp",EDGE,"E5.2.0");var subQ2=makeQuery(id+"F1.opExtrude","CAP_EDGE",EDGE,{"disambiguationData":[OSD([subQ1])],"isStart":true});Q10=makeQuery(id+"F4.imprint","IMPRINT",FACE,{"disambiguationData":[TD([[makeQuery(id+"F4.imprint","IMPRINT",EDGE,{"derivedFrom":subQ2}),-1.0]])]});}
            var Q11;
            {var subQ1=sQuery(id+"F0.wireOp",EDGE,"E5.1.0");var subQ2=makeQuery(id+"F1.opExtrude","CAP_EDGE",EDGE,{"disambiguationData":[OSD([subQ1])],"isStart":true});Q11=makeQuery(id+"F4.imprint","IMPRINT",FACE,{"disambiguationData":[TD([[makeQuery(id+"F4.imprint","IMPRINT",EDGE,{"derivedFrom":subQ2}),-1.0]])]});}
            var Q12;
            {var subQ1=sQuery(id+"F0.wireOp",EDGE,"E2");var subQ2=makeQuery(id+"F1.opExtrude","CAP_EDGE",EDGE,{"disambiguationData":[OSD([subQ1])],"isStart":true});Q12=makeQuery(id+"F4.imprint","IMPRINT",FACE,{"disambiguationData":[TD([[makeQuery(id+"F4.imprint","IMPRINT",EDGE,{"derivedFrom":subQ2}),-1.0]])]});}
            var Q13;
            {var subQ1=sQuery(id+"F0.wireOp",EDGE,"E4.MirrorCS");var subQ2=makeQuery(id+"F1.opExtrude","CAP_EDGE",EDGE,{"disambiguationData":[OSD([subQ1])],"isStart":true});Q13=makeQuery(id+"F4.imprint","IMPRINT",FACE,{"disambiguationData":[TD([[makeQuery(id+"F4.imprint","IMPRINT",EDGE,{"derivedFrom":subQ2}),1.0]])]});}
            var Q14;
            {var subQ1=sQuery(id+"F0.wireOp",EDGE,"E5.14.0");var subQ2=makeQuery(id+"F1.opExtrude","CAP_EDGE",EDGE,{"disambiguationData":[OSD([subQ1])],"isStart":true});Q14=makeQuery(id+"F4.imprint","IMPRINT",FACE,{"disambiguationData":[TD([[makeQuery(id+"F4.imprint","IMPRINT",EDGE,{"derivedFrom":subQ2}),-1.0]])]});}
            var Q15;
            {var subQ1=sQuery(id+"F0.wireOp",EDGE,"E5.13.0");var subQ2=makeQuery(id+"F1.opExtrude","CAP_EDGE",EDGE,{"disambiguationData":[OSD([subQ1])],"isStart":true});Q15=makeQuery(id+"F4.imprint","IMPRINT",FACE,{"disambiguationData":[TD([[makeQuery(id+"F4.imprint","IMPRINT",EDGE,{"derivedFrom":subQ2}),-1.0]])]});}
            var Q16;
            {var subQ26=sQuery(id+"F0.wireOp",EDGE,"E2");Q16=makeQuery(id+"F4.imprint","IMPRINT",FACE,{"disambiguationData":[TD([[makeQuery(id+"F4.imprint","IMPRINT",EDGE,{"derivedFrom":makeQuery(id+"F1.opExtrude","CAP_EDGE",EDGE,{"disambiguationData":[OSD([subQ26])],"isStart":true})}),1.0]])]});}
            extrude(context, id + "F5", {"entities" : qUnion([Q0, Q1, Q2, Q3, Q4, Q5, Q6, Q7, Q8, Q9, Q10, Q11, Q12, Q13, Q14, Q15, Q16]), "operationType" : NewBodyOperationType.ADD, "depth" : 3 * mm});
        }
        {
            var Q0;
            Q0=makeQuery(id+"F3.opExtrude","CAP_FACE",FACE,{"disambiguationData":[OSD([sQuery(id+"F2.wireOp",EDGE,"E6")])],"isStart":false});
            var sketch = newSketch(context, id + "F6", { "sketchPlane" : qUnion([Q0])});
            skCircle(sketch, "E8", {"center": v(0, 0) * mm, "radius": 12.5 * mm});
            skSolve(sketch);
        }
        {
            var Q0;
            Q0=makeQuery(id+"F6.imprint","IMPRINT",FACE,{"disambiguationData":[TD([[makeQuery(id+"F6.imprint","IMPRINT",EDGE,{"derivedFrom":sQuery(id+"F6.wireOp",EDGE,"E8")}),1.0]])]});
            extrude(context, id + "F7", {"entities" : qUnion([Q0]), "operationType" : NewBodyOperationType.REMOVE, "oppositeDirection" : true, "depth" : 4 * mm});
        }
    });
